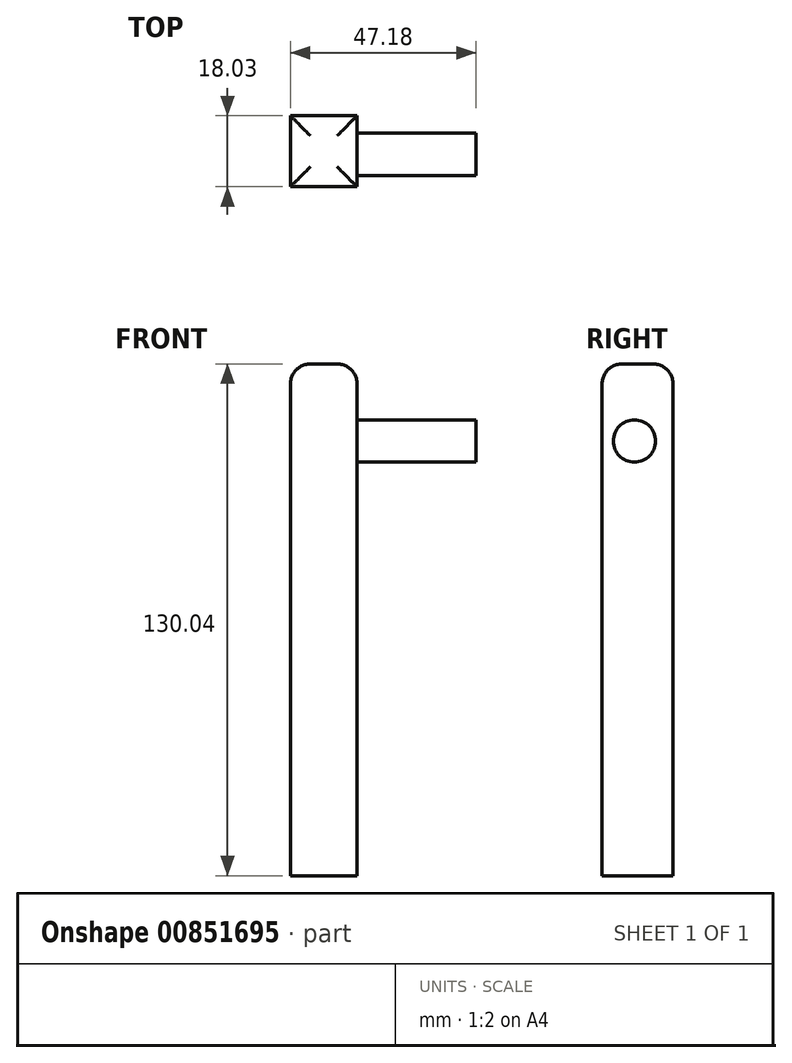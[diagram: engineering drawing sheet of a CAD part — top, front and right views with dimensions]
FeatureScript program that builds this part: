
annotation { "Feature Type Name" : "Feature", "Feature Type Description" : "" }
export const myFeature = defineFeature(function(context is Context, id is Id, definition is map)
    precondition{}
    {
        {
            var Q0;
            Q0=qCreatedBy(makeId("Front.planeOp"),FACE);
            var sketch = newSketch(context, id + "F0", { "sketchPlane" : qUnion([Q0])});
            skLineSegment(sketch, "E0.bottom", {"start": v(-16.95, 58.92) * mm, "end": v(0, 58.92) * mm});
            skLineSegment(sketch, "E0.top", {"start": v(-16.95, 0) * mm, "end": v(0, 0) * mm});
            skLineSegment(sketch, "E0.left", {"start": v(-16.95, 58.92) * mm, "end": v(-16.95, 0) * mm});
            skLineSegment(sketch, "E0.right", {"start": v(0, 58.92) * mm, "end": v(0, 0) * mm});
            skSolve(sketch);
        }
        {
            var Q0;
            Q0=makeQuery(id+"F0.imprint","IMPRINT",FACE,{"disambiguationData":[TD([[makeQuery(id+"F0.imprint","IMPRINT",EDGE,{"derivedFrom":sQuery(id+"F0.wireOp",EDGE,"E0.bottom")}),-1.0]])]});
            extrude(context, id + "F1", {"entities" : qUnion([Q0]), "depth" : 18.03 * mm, "offsetDistance" : 25.4 * mm});
        }
        {
            var Q0;
            Q0=makeQuery(id+"F1.opExtrude","SWEPT_FACE",FACE,{"disambiguationData":[OSD([sQuery(id+"F0.wireOp",EDGE,"E0.bottom")])]});
            extrude(context, id + "F2", {"entities" : qUnion([Q0]), "operationType" : NewBodyOperationType.ADD, "depth" : 71.12 * mm, "offsetDistance" : 25.4 * mm});
        }
        {
            var Q0;
            {var subQ0=sQuery(id+"F0.wireOp",EDGE,"E0.bottom");Q0=makeQuery(id+"F2.opExtrude","CAP_EDGE",EDGE,{"disambiguationData":[OSD([subQ0]),TDD([makeQuery(id+"F1.opExtrude","CAP_EDGE",EDGE,{"disambiguationData":[OSD([subQ0])],"isStart":false})])],"isStart":false});}
            var Q1;
            Q1=makeQuery(id+"F2.opExtrude","CAP_EDGE",EDGE,{"disambiguationData":[OSD([sQuery(id+"F0.wireOp",EDGE,"E0.bottom"),sQuery(id+"F0.wireOp",EDGE,"E0.right")])],"isStart":false});
            var Q2;
            {var subQ0=sQuery(id+"F0.wireOp",EDGE,"E0.bottom");Q2=makeQuery(id+"F2.opExtrude","CAP_EDGE",EDGE,{"disambiguationData":[OSD([subQ0]),TDD([makeQuery(id+"F1.opExtrude","CAP_EDGE",EDGE,{"disambiguationData":[OSD([subQ0])],"isStart":true})])],"isStart":false});}
            var Q3;
            Q3=makeQuery(id+"F2.opExtrude","CAP_EDGE",EDGE,{"disambiguationData":[OSD([sQuery(id+"F0.wireOp",EDGE,"E0.bottom"),sQuery(id+"F0.wireOp",EDGE,"E0.left")])],"isStart":false});
            fillet(context, id + "F3", {"entities" : qUnion([Q0, Q1, Q2, Q3]), "radius" : 5.08 * mm, "tangentPropagation" : true, "allowEdgeOverflow" : false});
        }
        {
            var Q0;
            {var subQ0=sQuery(id+"F0.wireOp",EDGE,"E0.right");Q0=makeQuery(id+"F2.boolean.opBoolean","MERGE",FACE,{"derivedFrom":[makeQuery(id+"F1.opExtrude","SWEPT_FACE",FACE,{"disambiguationData":[OSD([subQ0])]}),makeQuery(id+"F2.opExtrude","SWEPT_FACE",FACE,{"disambiguationData":[OSD([sQuery(id+"F0.wireOp",EDGE,"E0.bottom"),subQ0])]})]});}
            var sketch = newSketch(context, id + "F4", { "sketchPlane" : qUnion([Q0])});
            skCircle(sketch, "E1", {"center": v(-9.8, 110.43) * mm, "radius": 5.37 * mm});
            skSolve(sketch);
        }
        {
            var Q0;
            Q0=makeQuery(id+"F4.imprint","IMPRINT",FACE,{"disambiguationData":[TD([[makeQuery(id+"F4.imprint","IMPRINT",EDGE,{"derivedFrom":sQuery(id+"F4.wireOp",EDGE,"E1")}),1.0]])]});
            extrude(context, id + "F5", {"entities" : qUnion([Q0]), "operationType" : NewBodyOperationType.ADD, "depth" : 30.23 * mm, "offsetDistance" : 25.4 * mm});
        }
    });
